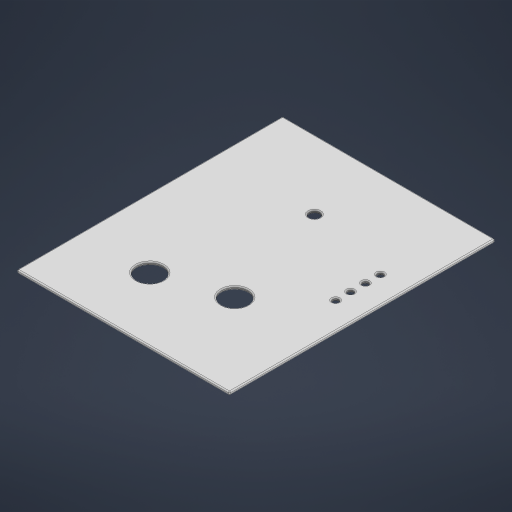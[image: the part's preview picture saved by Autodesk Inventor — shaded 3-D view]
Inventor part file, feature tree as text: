
AUTODESK INVENTOR PART (.ipt)
format: ipt  version: 2023 (Build 270158000, 158)  size: 260,608 bytes
history: native  units: mm
features: extrude x1, fillet x1, other x1
ambient origin geometry x8: Origin, YZ Plane, XZ Plane, XY Plane, X Axis, Y Axis, Z Axis, Center Point
bodies: Solid1 (feature_tree)
feature tree (3):
  extrude  "nand"  Depth=200.0mm
  fillet  "Fillet1"  Radius=250.0mm
  other  "page_lines"
